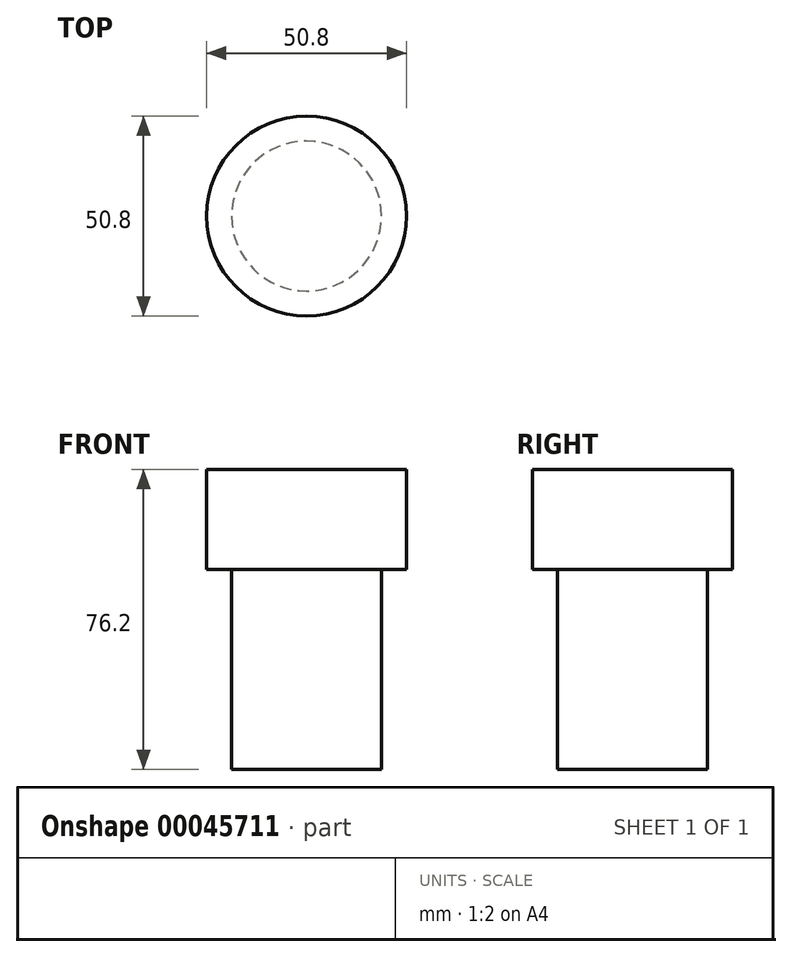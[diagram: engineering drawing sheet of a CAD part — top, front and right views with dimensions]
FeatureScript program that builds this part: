
annotation { "Feature Type Name" : "Feature", "Feature Type Description" : "" }
export const myFeature = defineFeature(function(context is Context, id is Id, definition is map)
    precondition{}
    {
        {
            var Q0;
            Q0=qCreatedBy(makeId("Front.planeOp"),FACE);
            var sketch = newSketch(context, id + "F0", { "sketchPlane" : qUnion([Q0])});
            skLineSegment(sketch, "E0", {"start": v(0, 41.87) * mm, "end": v(25.4, 41.87) * mm});
            skLineSegment(sketch, "E1", {"start": v(25.4, 41.87) * mm, "end": v(25.4, 16.47) * mm});
            skLineSegment(sketch, "E2", {"start": v(25.4, 16.47) * mm, "end": v(19.05, 16.47) * mm});
            skLineSegment(sketch, "E3", {"start": v(19.05, 16.47) * mm, "end": v(19.05, -34.33) * mm});
            skLineSegment(sketch, "E4", {"start": v(19.05, -34.33) * mm, "end": v(0, -34.33) * mm});
            skLineSegment(sketch, "E5", {"start": v(0, -34.33) * mm, "end": v(0, 41.87) * mm});
            skSolve(sketch);
        }
        {
            var Q0;
            Q0=makeQuery(id+"F0.imprint","IMPRINT",FACE,{"disambiguationData":[TD([[makeQuery(id+"F0.imprint","IMPRINT",EDGE,{"derivedFrom":sQuery(id+"F0.wireOp",EDGE,"E0")}),-1.0]])]});
            var Q1;
            Q1=sQuery(id+"F0.wireOp",EDGE,"E5");
            revolve(context, id + "F1", {"entities" : qUnion([Q0]), "axis" : qUnion([Q1]), "revolveType" : RevolveType.FULL});
        }
    });
